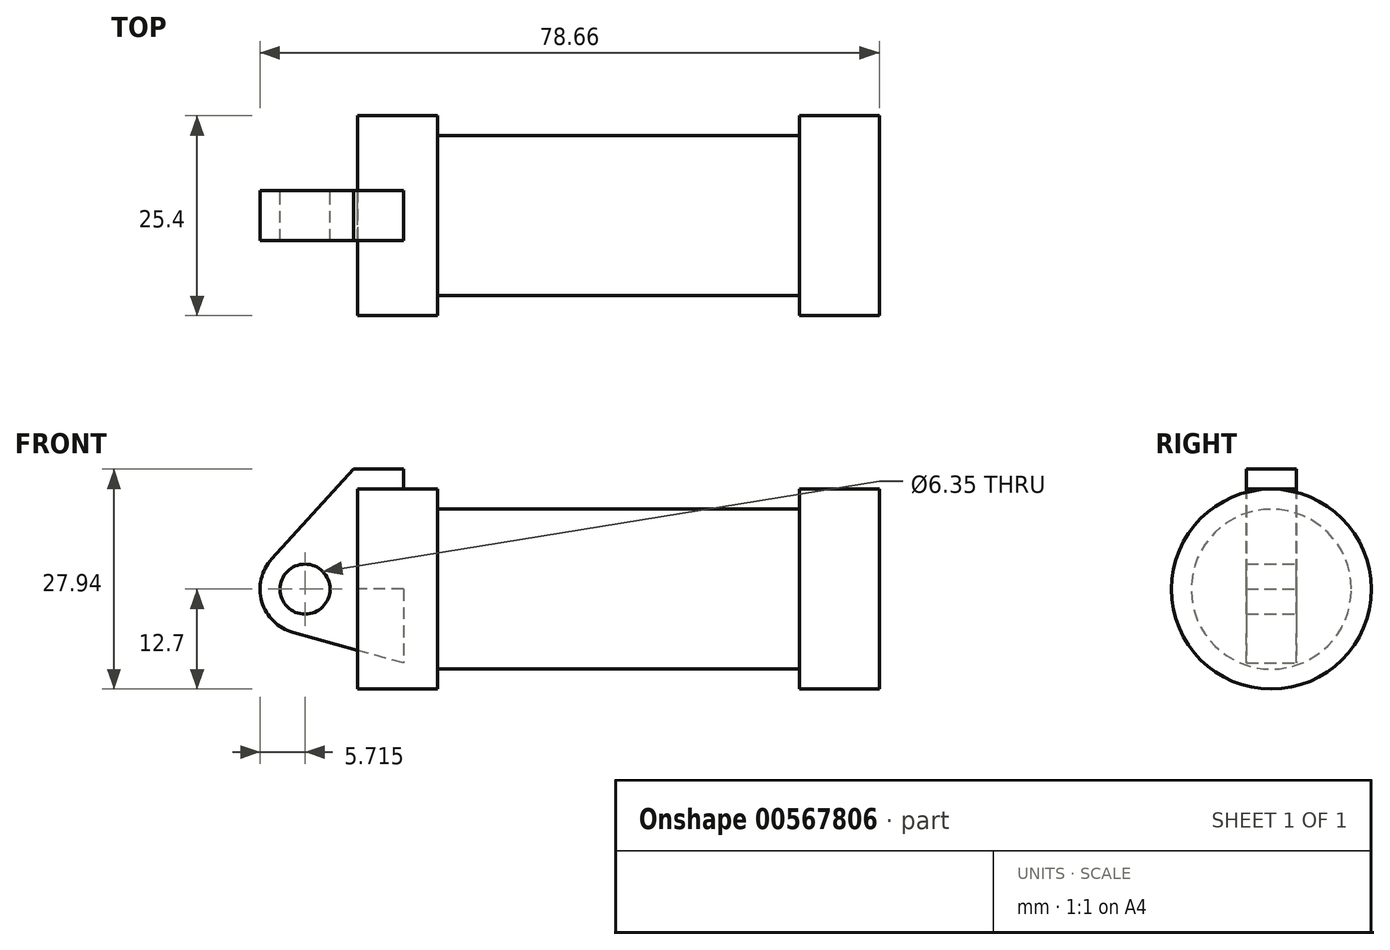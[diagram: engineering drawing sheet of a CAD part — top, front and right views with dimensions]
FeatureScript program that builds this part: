
annotation { "Feature Type Name" : "Feature", "Feature Type Description" : "" }
export const myFeature = defineFeature(function(context is Context, id is Id, definition is map)
    precondition{}
    {
        {
            var Q0;
            Q0=qCreatedBy(makeId("Front.planeOp"),FACE);
            var sketch = newSketch(context, id + "F0", { "sketchPlane" : qUnion([Q0])});
            skLineSegment(sketch, "E0", {"start": v(0, 0) * mm, "end": v(0, 12.7) * mm});
            skLineSegment(sketch, "E1", {"start": v(0, 12.7) * mm, "end": v(10.16, 12.7) * mm});
            skLineSegment(sketch, "E2", {"start": v(10.16, 12.7) * mm, "end": v(10.16, 10.16) * mm});
            skLineSegment(sketch, "E3", {"start": v(10.16, 10.16) * mm, "end": v(56.13, 10.16) * mm});
            skLineSegment(sketch, "E4", {"start": v(56.13, 10.16) * mm, "end": v(56.13, 12.7) * mm});
            skLineSegment(sketch, "E5", {"start": v(56.13, 12.7) * mm, "end": v(66.3, 12.7) * mm});
            skLineSegment(sketch, "E6", {"start": v(66.3, 12.7) * mm, "end": v(66.3, 0) * mm});
            skLineSegment(sketch, "E7", {"start": v(66.3, 0) * mm, "end": v(0, 0) * mm});
            skLineSegment(sketch, "E8", {"start": v(5.84, 15.24) * mm, "end": v(-0.5, 15.24) * mm});
            skLineSegment(sketch, "E9", {"start": v(-0.5, 15.24) * mm, "end": v(-10.88, 3.85) * mm});
            skLineSegment(sketch, "E10", {"start": v(0, 0) * mm, "end": v(-6.65, 0) * mm});
            skCircle(sketch, "E11", {"center": v(-6.65, 0) * mm, "radius": 5.72 * mm});
            skCircle(sketch, "E12", {"center": v(-6.65, 0) * mm, "radius": 3.18 * mm});
            skLineSegment(sketch, "E13", {"start": v(5.84, 15.24) * mm, "end": v(5.84, -9.4) * mm});
            skLineSegment(sketch, "E14", {"start": v(5.84, -9.4) * mm, "end": v(-8.18, -5.5) * mm});
            skSolve(sketch);
        }
        {
            var Q0;
            {var subQ0=sQuery(id+"F0.wireOp",EDGE,"E2");Q0=makeQuery(id+"F0.imprint","IMPRINT",FACE,{"disambiguationData":[TD([[makeQuery(id+"F0.imprint","IMPRINT",EDGE,{"derivedFrom":subQ0}),-1.0]])]});}
            var Q1;
            {var subQ0=sQuery(id+"F0.wireOp",EDGE,"E0");Q1=makeQuery(id+"F0.imprint","IMPRINT",FACE,{"disambiguationData":[TD([[makeQuery(id+"F0.imprint","IMPRINT",EDGE,{"derivedFrom":subQ0}),-1.0]])]});}
            var Q2;
            Q2=sQuery(id+"F0.wireOp",EDGE,"E7");
            revolve(context, id + "F1", {"entities" : qUnion([Q0, Q1]), "axis" : qUnion([Q2]), "revolveType" : RevolveType.FULL});
        }
        {
            var Q0;
            {var subQ1=sQuery(id+"F0.wireOp",EDGE,"E0");Q0=makeQuery(id+"F0.imprint","IMPRINT",FACE,{"disambiguationData":[TD([[makeQuery(id+"F0.imprint","IMPRINT",EDGE,{"derivedFrom":subQ1}),1.0]])]});}
            var Q1;
            {var subQ0=sQuery(id+"F0.wireOp",EDGE,"E14");Q1=makeQuery(id+"F0.imprint","IMPRINT",FACE,{"disambiguationData":[TD([[makeQuery(id+"F0.imprint","IMPRINT",EDGE,{"derivedFrom":subQ0}),-1.0]])]});}
            var Q2;
            {var subQ5=sQuery(id+"F0.wireOp",EDGE,"E12");Q2=makeQuery(id+"F0.imprint","IMPRINT",FACE,{"disambiguationData":[TD([[makeQuery(id+"F0.imprint","IMPRINT",EDGE,{"derivedFrom":subQ5}),-1.0]])]});}
            extrude(context, id + "F2", {"entities" : qUnion([Q0, Q1, Q2]), "endBound" : BoundingType.SYMMETRIC, "depth" : 6.35 * mm, "offsetDistance" : 25.4 * mm});
        }
    });
